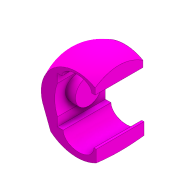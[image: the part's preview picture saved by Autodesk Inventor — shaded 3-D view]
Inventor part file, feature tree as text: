
AUTODESK INVENTOR PART (.ipt)
format: ipt  version: 2020 (Build 240168000, 168)  size: 999,424 bytes
history: native  units: mm
features: sketch x7, extrude x4, plane x3, other x3, loft x1, direct_edit x1, projected_geometry x1
ambient origin geometry x8: Origin, YZ Plane, XZ Plane, XY Plane, X Axis, Y Axis, Z Axis, Center Point
bodies: Solid1 (feature_tree)
feature tree (20):
  sketch  "Sketch1"  dims[d16=4.5mm d17=4.5mm]
  plane  "Work Plane1"
  sketch  "Sketch2"  dims[d19=0.0mm d20=90.0deg d21=0.0mm d22=90.0deg]
  plane  "Work Plane2"
  loft  "Loft1"
  extrude  "Extrusion1"  TaperAngle=0.0deg  [1 undecoded]
  plane  "Work Plane3"
  extrude  "Extrusion2"  Depth=0.2mm
  extrude  "Extrusion3"  Depth=5.0mm
  direct_edit  "Direct Edit1"
  extrude  "Extrusion4"  Depth=4.5mm TaperAngle=0.0deg
  other  "Image1"
  sketch  "Sketch3"  dims[d23=0.0mm d24=90.0deg d32=0.2mm]
  sketch  "Sketch4"  dims[d34=10.0mm d35=0.0mm d36=5.0mm]
  other  "Image2"
  sketch  "Sketch5"  dims[d37=10.0mm d38=0.0mm d39=4.5mm d40=0.0mm]
  projected_geometry  "Projected Loop1"
  sketch  "Sketch6"  dims[d41=8.0mm d42=10.0mm d43=10.0mm]
  sketch  "Sketch7"  dims[d44=10.0mm d45=0.0mm d33=0.5mm]
  other  "Scale1"
note: 1 required parameter value undecoded (feature->parameter linkage not recoverable at this tier; creation-order binding heuristic only, values carry confidence <= 0.55)
